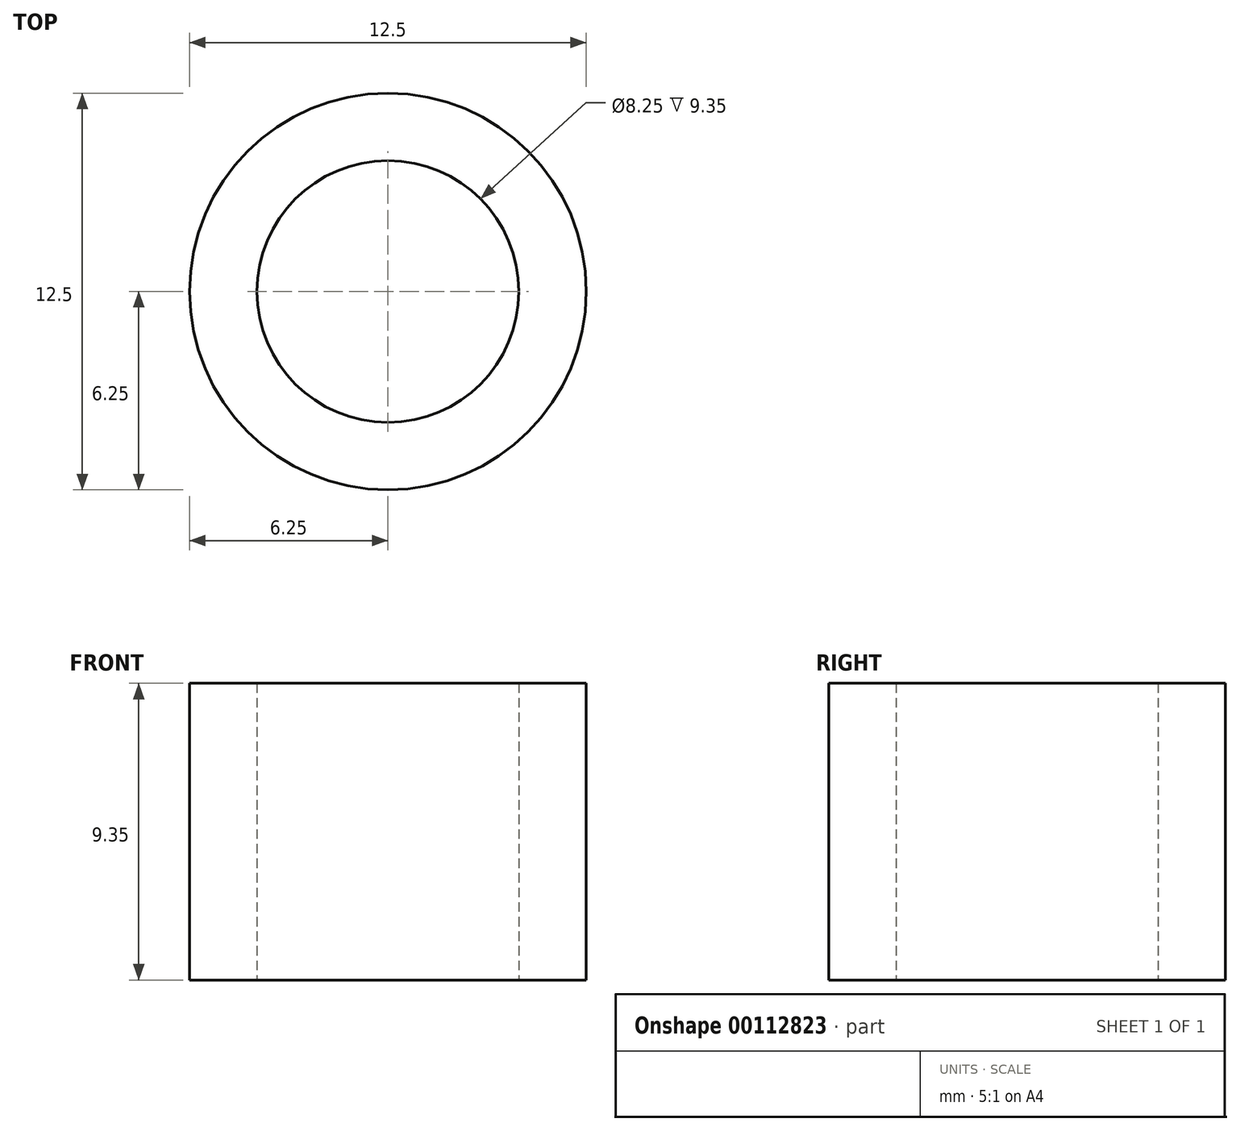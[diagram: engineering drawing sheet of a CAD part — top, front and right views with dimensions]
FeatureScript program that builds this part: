
annotation { "Feature Type Name" : "Feature", "Feature Type Description" : "" }
export const myFeature = defineFeature(function(context is Context, id is Id, definition is map)
    precondition{}
    {
        {
            var Q0;
            Q0=qCreatedBy(makeId("Top.planeOp"),FACE);
            var sketch = newSketch(context, id + "F0", { "sketchPlane" : qUnion([Q0])});
            skCircle(sketch, "E0", {"center": v(0, 0) * mm, "radius": 6.25 * mm});
            skCircle(sketch, "E1", {"center": v(0, 0) * mm, "radius": 4.12 * mm});
            skSolve(sketch);
        }
        {
            var Q0;
            Q0 = qSketchRegion(id + "F0", true);
            extrude(context, id + "F1", {"entities" : qUnion([Q0]), "depth" : 9.35 * mm});
        }
    });
